# Revit family: Legrand coffret encastré métallique triphasé British standard
name_source: partatom
category: Equipement électrique
revit_build: Autodesk Revit 2018 (Build: 20170223_1515(x64)
units: mm (PartAtom-declared; Revit-internal decimal feet)

## family parameters
Basée sur le plan de construction = Non
Configuration du panneau = Deux colonnes, circuits au sein
Cote de connecteur circulaire = Utiliser le diamètre
Couper avec des vides une fois chargée = Non
Numéro OmniClass = 23.80.30.11.17
Partagée = Non
Point de calcul de pièce = Non
Titre OmniClass = Distribution Boards and Control Panels
Toujours verticalement = Oui
Type d'élément = Tableau de raccordement

## types (4) — shared parameters
Conditions Générale d'Utilisation = https://export.legrand.com
Couleur = Gris
Fabricant = Legrand
Hauteur = 415 mm  [stored 1.36155 ft]
Matière = Métal
Modèle = Flush-mounting British standard
Puissance = 100A
URL = www.legrand.com
profondeur = 82 mm  [stored 0.269029 ft]

## per-type parameters (varying)
| type | 402515 | 402516 | 402517 | 402518 | Bornier N | Bornier T | Largeur | nombre de modules 3P |
| Coffret 402515 | Oui | Non | Non | Non | 3X4 trous | 3X4 trous | 305 mm  [stored 1.00066 ft] | 4 |
| Coffret 402516 | Non | Oui | Non | Non | 3X6 trous | 3X6 trous | 341 mm | 6 |
| Coffret 402517 | Non | Non | Oui | Non | 3X8 trous | 3X8 trous | 425 mm  [stored 1.39436 ft] | 8 |
| Coffret 402518 | Non | Non | Non | Oui | 3X12 trous | 3X12 trous | 569 mm  [stored 1.8668 ft] | 12 |

note: [stored X ft] marks values corroborated as IEEE doubles in the binary element streams (Revit-internal decimal feet)
